# Revit family: ShowerBase_ProBase_NobleCompany
name_source: partatom
category: Specialty Equipment
revit_build: Autodesk Revit 2015 (Build: 20140606_1530(x64)
units: mm (PartAtom-declared; Revit-internal decimal feet)

## types (3) — shared parameters
Assembly Code = D2030300
Base = Polypropylene - High Strength
Building Codes = http://www.noblecompany.com
Default Elevation = 0"
Drain Hole Diameter = 3"
Hang = 1/8"
Installation-Fabrication = http://www.noblecompany.com
Manufacturer = Noble Company
Manufacturer Fax = 231-799-8850
Panel Size = 16"
Product Data = http://www.noblecompany.com
Product Properties = http://www.noblecompany.com
URL = www.noblecompany.com

## per-type parameters (varying)
| type | Depth | Description | DrainLoc | Height | Model | Width |
| 48x48 | 48" | Noble Pro Base Shower Base | 24" | 1 5/8" | Pro Base 4848 | 48" |
| 32x60 Center Drain | 32" | Noble Pro Slope Shower Base | 30" | 1 5/8" | Pro Base 3260 Center | 60" |
| 32x60 End Drain | 32" | Noble Pro Slope Shower Base | 12" | 2 1/16" | Pro Base 3260 End | 60" |

## geometry (parser evidence)
native form markers: Sweep x2
no freeform markers — native parametric forms only
